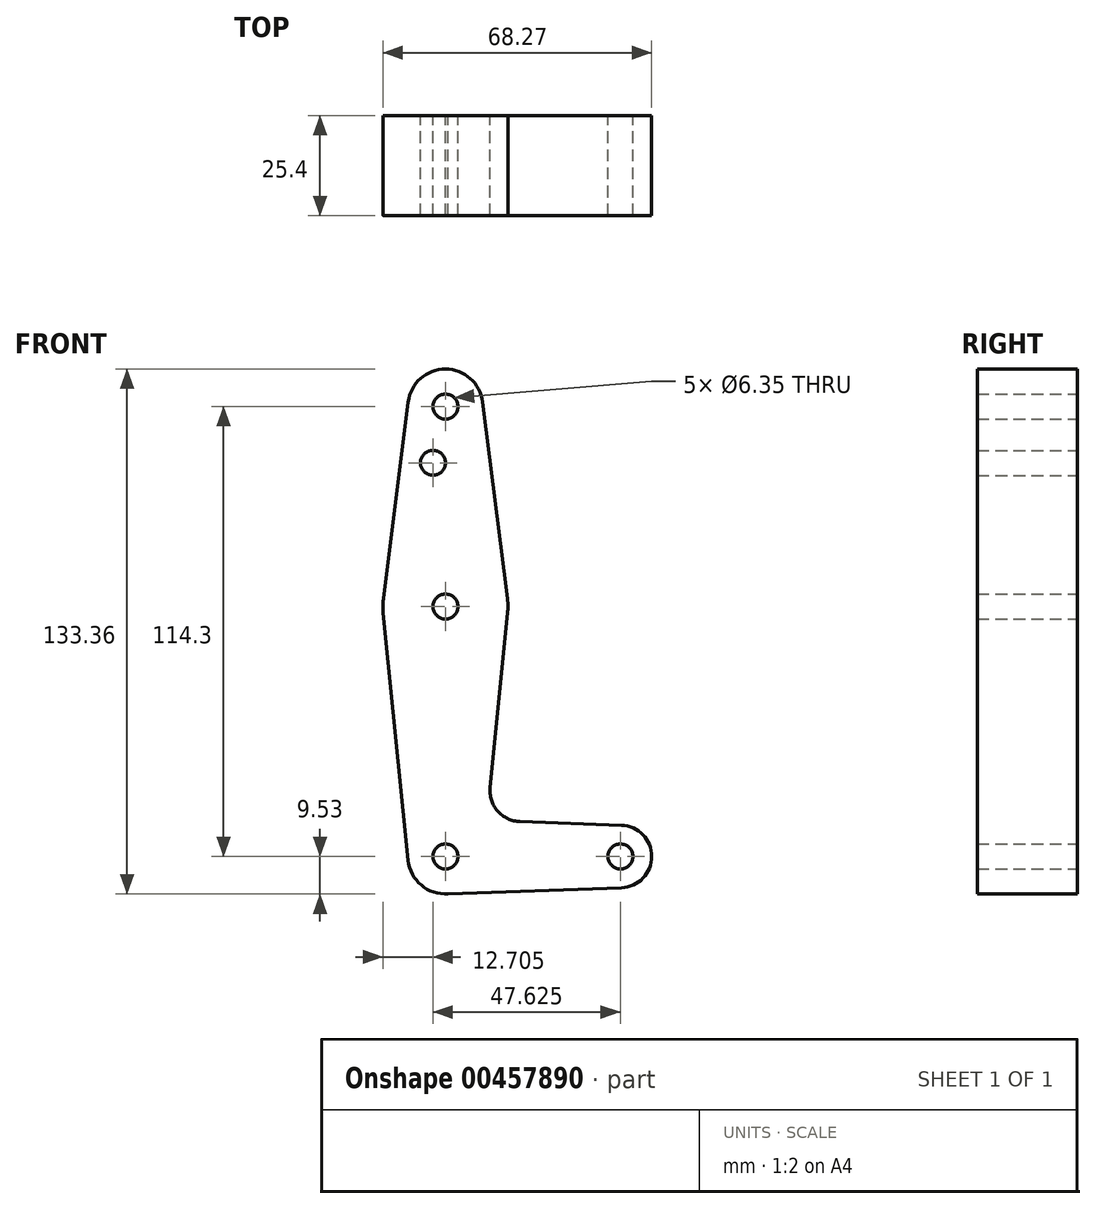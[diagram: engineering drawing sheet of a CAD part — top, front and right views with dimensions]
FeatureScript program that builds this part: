
annotation { "Feature Type Name" : "Feature", "Feature Type Description" : "" }
export const myFeature = defineFeature(function(context is Context, id is Id, definition is map)
    precondition{}
    {
        {
            var Q0;
            Q0=qCreatedBy(makeId("Front.planeOp"),FACE);
            var sketch = newSketch(context, id + "F0", { "sketchPlane" : qUnion([Q0])});
            skLineSegment(sketch, "E0", {"start": v(0, 0) * mm, "end": v(0, 114.3) * mm, "construction": true});
            skLineSegment(sketch, "E1", {"start": v(0, 0) * mm, "end": v(44.45, 0) * mm, "construction": true});
            skCircle(sketch, "E2", {"center": v(0, 114.3) * mm, "radius": 9.53 * mm});
            skCircle(sketch, "E3", {"center": v(0, 63.5) * mm, "radius": 15.88 * mm});
            skCircle(sketch, "E4", {"center": v(0, 0) * mm, "radius": 9.53 * mm});
            skCircle(sketch, "E5", {"center": v(44.45, 0) * mm, "radius": 7.94 * mm});
            skLineSegment(sketch, "E6", {"start": v(0, -9.53) * mm, "end": v(44.73, -7.93) * mm});
            skLineSegment(sketch, "E7.MirrorCS", {"start": v(18.97, 8.85) * mm, "end": v(44.73, 7.93) * mm});
            skLineSegment(sketch, "E8", {"start": v(-9.45, 115.5) * mm, "end": v(-15.75, 65.48) * mm});
            skLineSegment(sketch, "E9.MirrorCS", {"start": v(9.45, 115.5) * mm, "end": v(15.75, 65.48) * mm});
            skCircle(sketch, "E10", {"center": v(0, 114.3) * mm, "radius": 3.18 * mm});
            skCircle(sketch, "E11", {"center": v(0, 63.5) * mm, "radius": 3.18 * mm});
            skCircle(sketch, "E12", {"center": v(0, 0) * mm, "radius": 3.18 * mm});
            skCircle(sketch, "E13", {"center": v(44.45, 0) * mm, "radius": 3.18 * mm});
            skCircle(sketch, "E14", {"center": v(-3.18, 100.03) * mm, "radius": 3.18 * mm});
            skLineSegment(sketch, "E15", {"start": v(-15.8, 61.91) * mm, "end": v(-9.48, -0.95) * mm});
            skLineSegment(sketch, "E16.MirrorCS", {"start": v(15.8, 61.91) * mm, "end": v(11.34, 17.59) * mm});
            skPoint(sketch, "E17.newPointA", {"position": v(9.48, -0.95) * mm});
            skPoint(sketch, "E17.newPointB", {"position": v(0, 9.53) * mm});
            skArc(sketch, "E17.filletArc", {"start": v(11.34, 17.59) * mm, "mid": v(13.26, 11.57) * mm, "end": v(18.97, 8.85) * mm});
            skSolve(sketch);
        }
        {
            var Q0;
            Q0 = qSketchRegion(id + "F0", true);
            extrude(context, id + "F1", {"entities" : qUnion([Q0]), "depth" : 25.4 * mm});
        }
    });
